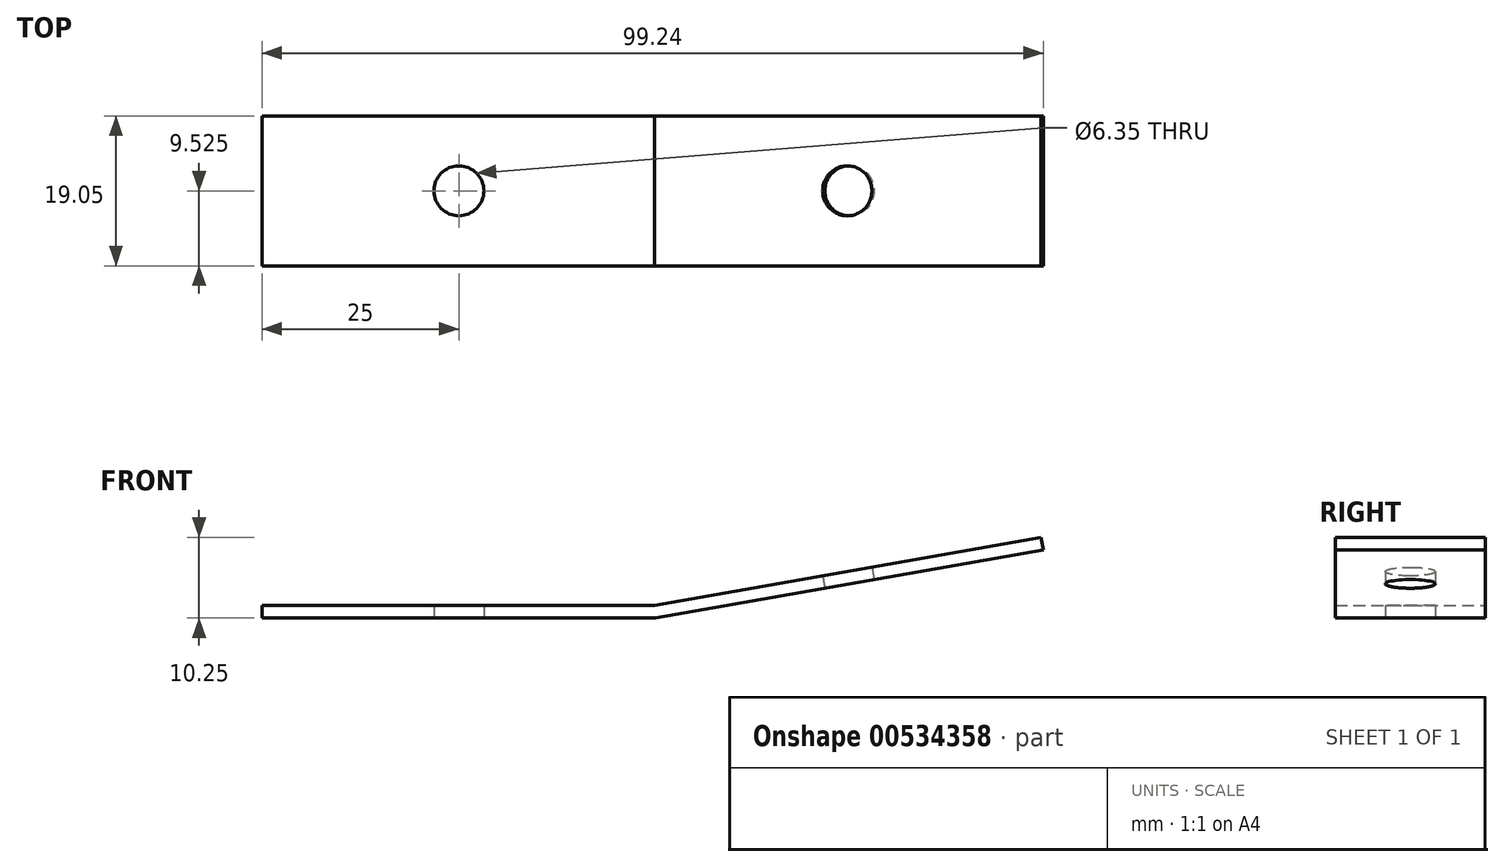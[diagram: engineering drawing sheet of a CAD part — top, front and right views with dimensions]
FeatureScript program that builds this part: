
annotation { "Feature Type Name" : "Feature", "Feature Type Description" : "" }
export const myFeature = defineFeature(function(context is Context, id is Id, definition is map)
    precondition{}
    {
        {
            var Q0;
            Q0=qCreatedBy(makeId("Front.planeOp"),FACE);
            var sketch = newSketch(context, id + "F0", { "sketchPlane" : qUnion([Q0])});
            skLineSegment(sketch, "E0", {"start": v(0, 0) * mm, "end": v(50, 0) * mm});
            skLineSegment(sketch, "E1", {"start": v(99.24, 8.68) * mm, "end": v(50, 0) * mm});
            skLineSegment(sketch, "E2", {"start": v(98.96, 10.25) * mm, "end": v(99.24, 8.68) * mm});
            skLineSegment(sketch, "E3", {"start": v(49.86, 1.59) * mm, "end": v(98.96, 10.25) * mm});
            skLineSegment(sketch, "E4", {"start": v(49.86, 1.59) * mm, "end": v(0, 1.59) * mm});
            skLineSegment(sketch, "E5", {"start": v(0, 1.59) * mm, "end": v(0, 0) * mm});
            skSolve(sketch);
        }
        {
            var Q0;
            Q0=makeQuery(id+"F0.imprint","IMPRINT",FACE,{"disambiguationData":[TD([[makeQuery(id+"F0.imprint","IMPRINT",EDGE,{"derivedFrom":sQuery(id+"F0.wireOp",EDGE,"E0")}),1.0]])]});
            extrude(context, id + "F1", {"entities" : qUnion([Q0]), "depth" : 19.05 * mm, "offsetDistance" : 25 * mm});
        }
        {
            var Q0;
            Q0=makeQuery(id+"F1.opExtrude","SWEPT_FACE",FACE,{"disambiguationData":[OSD([sQuery(id+"F0.wireOp",EDGE,"E0")])]});
            var sketch = newSketch(context, id + "F2", { "sketchPlane" : qUnion([Q0])});
            skCircle(sketch, "E6", {"center": v(25, 9.53) * mm, "radius": 3.17 * mm});
            skPoint(sketch, "E7", {"position": v(0, 9.53) * mm});
            skSolve(sketch);
        }
        {
            var Q0;
            Q0=makeQuery(id+"F2.imprint","IMPRINT",FACE,{"disambiguationData":[TD([[makeQuery(id+"F2.imprint","IMPRINT",EDGE,{"derivedFrom":sQuery(id+"F2.wireOp",EDGE,"E6")}),1.0]])]});
            extrude(context, id + "F3", {"entities" : qUnion([Q0]), "operationType" : NewBodyOperationType.REMOVE, "oppositeDirection" : true, "depth" : 25 * mm, "offsetDistance" : 25 * mm});
        }
        {
            var Q0;
            Q0=makeQuery(id+"F1.opExtrude","SWEPT_FACE",FACE,{"disambiguationData":[OSD([sQuery(id+"F0.wireOp",EDGE,"E1")])]});
            var sketch = newSketch(context, id + "F4", { "sketchPlane" : qUnion([Q0])});
            skCircle(sketch, "E8", {"center": v(74.24, 9.53) * mm, "radius": 3.17 * mm});
            skPoint(sketch, "E9", {"position": v(99.24, 9.53) * mm});
            skSolve(sketch);
        }
        {
            var Q0;
            Q0=makeQuery(id+"F4.imprint","IMPRINT",FACE,{"disambiguationData":[TD([[makeQuery(id+"F4.imprint","IMPRINT",EDGE,{"derivedFrom":sQuery(id+"F4.wireOp",EDGE,"E8")}),1.0]])]});
            extrude(context, id + "F5", {"entities" : qUnion([Q0]), "operationType" : NewBodyOperationType.REMOVE, "oppositeDirection" : true, "depth" : 25 * mm, "offsetDistance" : 25 * mm});
        }
    });
